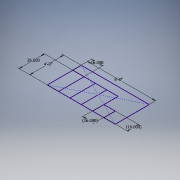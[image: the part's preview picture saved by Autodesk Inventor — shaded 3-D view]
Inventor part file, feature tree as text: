
AUTODESK INVENTOR PART (.ipt)
format: ipt  version: 2017 SP1 (Build 210196100, 196)  size: 95,232 bytes
history: native  units: in
note: dims shown in document units (in); Inventor stores cm internally (conversion verified against a paired STEP export)
features: sketch x1
ambient origin geometry x8: Origin, YZ Plane, XZ Plane, XY Plane, X Axis, Y Axis, Z Axis, Center Point
feature tree (1):
  sketch  "Sketch1"  dims[d0=96.0in d1=48.0in d2=16.0in d3=36.0in d4=16.0in d5=16.0in]
